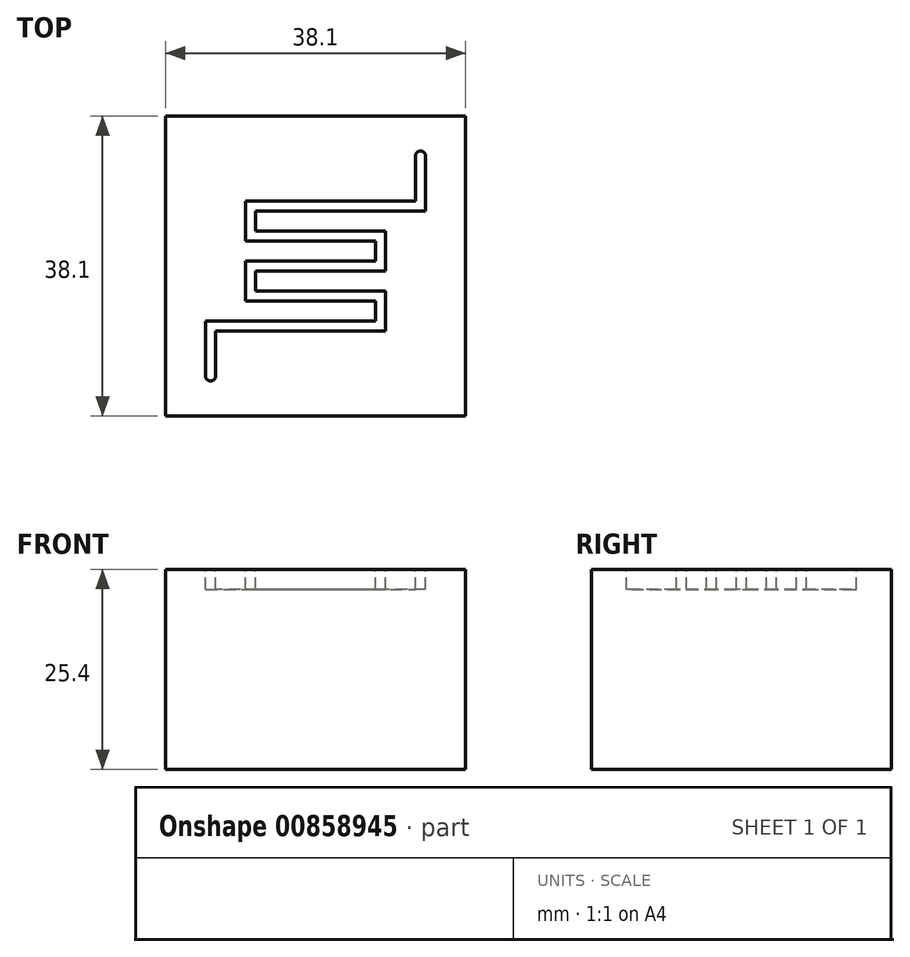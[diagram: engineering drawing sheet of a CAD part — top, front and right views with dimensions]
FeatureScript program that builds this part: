
annotation { "Feature Type Name" : "Feature", "Feature Type Description" : "" }
export const myFeature = defineFeature(function(context is Context, id is Id, definition is map)
    precondition{}
    {
        {
            var Q0;
            Q0=qCreatedBy(makeId("Top.planeOp"),FACE);
            var sketch = newSketch(context, id + "F0", { "sketchPlane" : qUnion([Q0])});
            skLineSegment(sketch, "E0.bottom", {"start": v(-19.05, -19.05) * mm, "end": v(19.05, -19.05) * mm});
            skLineSegment(sketch, "E0.top", {"start": v(-19.05, 19.05) * mm, "end": v(19.05, 19.05) * mm});
            skLineSegment(sketch, "E0.left", {"start": v(-19.05, -19.05) * mm, "end": v(-19.05, 19.05) * mm});
            skLineSegment(sketch, "E0.right", {"start": v(19.05, -19.05) * mm, "end": v(19.05, 19.05) * mm});
            skLineSegment(sketch, "E1", {"start": v(0, 0) * mm, "end": v(19.05, 0) * mm, "construction": true});
            skLineSegment(sketch, "E2", {"start": v(0, 0) * mm, "end": v(0, 19.05) * mm, "construction": true});
            skSolve(sketch);
        }
        {
            var Q0;
            Q0 = qSketchRegion(id + "F0", true);
            extrude(context, id + "F1", {"entities" : qUnion([Q0]), "depth" : 25.4 * mm, "offsetDistance" : 25.4 * mm});
        }
        {
            var Q0;
            Q0=makeQuery(id+"F1.opExtrude","CAP_FACE",FACE,{"disambiguationData":[OSD([sQuery(id+"F0.wireOp",EDGE,"E0.bottom"),sQuery(id+"F0.wireOp",EDGE,"E0.top"),sQuery(id+"F0.wireOp",EDGE,"E0.left"),sQuery(id+"F0.wireOp",EDGE,"E0.right")])],"isStart":false});
            var sketch = newSketch(context, id + "F2", { "sketchPlane" : qUnion([Q0])});
            skLineSegment(sketch, "E3", {"start": v(-13.97, -13.97) * mm, "end": v(-13.97, -6.99) * mm});
            skLineSegment(sketch, "E4", {"start": v(-13.97, -6.99) * mm, "end": v(7.62, -6.99) * mm});
            skLineSegment(sketch, "E5", {"start": v(7.62, -6.99) * mm, "end": v(7.62, -4.45) * mm});
            skLineSegment(sketch, "E6", {"start": v(7.62, -4.45) * mm, "end": v(-8.9, -4.45) * mm});
            skLineSegment(sketch, "E7", {"start": v(-8.9, -4.45) * mm, "end": v(-8.9, 0.63) * mm});
            skLineSegment(sketch, "E8", {"start": v(-8.9, 0.63) * mm, "end": v(7.62, 0.63) * mm});
            skLineSegment(sketch, "E9", {"start": v(7.62, 0.63) * mm, "end": v(7.62, 3.18) * mm});
            skLineSegment(sketch, "E10", {"start": v(7.62, 3.18) * mm, "end": v(-8.9, 3.17) * mm});
            skLineSegment(sketch, "E11", {"start": v(-8.9, 3.17) * mm, "end": v(-8.9, 8.26) * mm});
            skLineSegment(sketch, "E12", {"start": v(12.7, 8.25) * mm, "end": v(12.7, 13.97) * mm});
            skLineSegment(sketch, "E13", {"start": v(12.7, 13.97) * mm, "end": v(13.97, 13.97) * mm, "construction": true});
            skLineSegment(sketch, "E14", {"start": v(13.97, 13.97) * mm, "end": v(13.97, 6.99) * mm});
            skLineSegment(sketch, "E15", {"start": v(13.97, 6.99) * mm, "end": v(-7.62, 6.99) * mm});
            skLineSegment(sketch, "E16", {"start": v(-7.62, 6.99) * mm, "end": v(-7.62, 4.45) * mm});
            skLineSegment(sketch, "E17", {"start": v(-7.62, 4.45) * mm, "end": v(8.9, 4.45) * mm});
            skLineSegment(sketch, "E18", {"start": v(8.9, 4.45) * mm, "end": v(8.9, -0.64) * mm});
            skLineSegment(sketch, "E19", {"start": v(8.9, -0.64) * mm, "end": v(-7.62, -0.64) * mm});
            skLineSegment(sketch, "E20", {"start": v(-7.62, -0.64) * mm, "end": v(-7.62, -3.18) * mm});
            skLineSegment(sketch, "E21", {"start": v(-7.62, -3.18) * mm, "end": v(8.9, -3.18) * mm});
            skLineSegment(sketch, "E22", {"start": v(8.9, -3.18) * mm, "end": v(8.9, -8.26) * mm});
            skLineSegment(sketch, "E23", {"start": v(8.9, -8.26) * mm, "end": v(-12.7, -8.26) * mm});
            skLineSegment(sketch, "E24", {"start": v(-12.7, -8.26) * mm, "end": v(-12.7, -13.97) * mm});
            skLineSegment(sketch, "E25", {"start": v(-12.7, -13.97) * mm, "end": v(-13.97, -13.97) * mm, "construction": true});
            skLineSegment(sketch, "E26", {"start": v(-8.9, 8.26) * mm, "end": v(12.7, 8.26) * mm});
            skLineSegment(sketch, "E27", {"start": v(7.62, -6.99) * mm, "end": v(7.62, -8.26) * mm, "construction": true});
            skLineSegment(sketch, "E28", {"start": v(7.62, -6.99) * mm, "end": v(8.9, -6.99) * mm, "construction": true});
            skLineSegment(sketch, "E29", {"start": v(-7.62, -3.18) * mm, "end": v(-8.9, -3.18) * mm, "construction": true});
            skArc(sketch, "E30", {"start": v(-13.97, -13.97) * mm, "mid": v(-13.34, -14.6) * mm, "end": v(-12.7, -13.97) * mm});
            skArc(sketch, "E31", {"start": v(13.97, 13.97) * mm, "mid": v(13.34, 14.6) * mm, "end": v(12.7, 13.97) * mm});
            skSolve(sketch);
        }
        {
            var Q0;
            Q0 = qSketchRegion(id + "F2", true);
            extrude(context, id + "F3", {"entities" : qUnion([Q0]), "operationType" : NewBodyOperationType.REMOVE, "oppositeDirection" : true, "depth" : 2.54 * mm, "offsetDistance" : 25.4 * mm});
        }
    });
